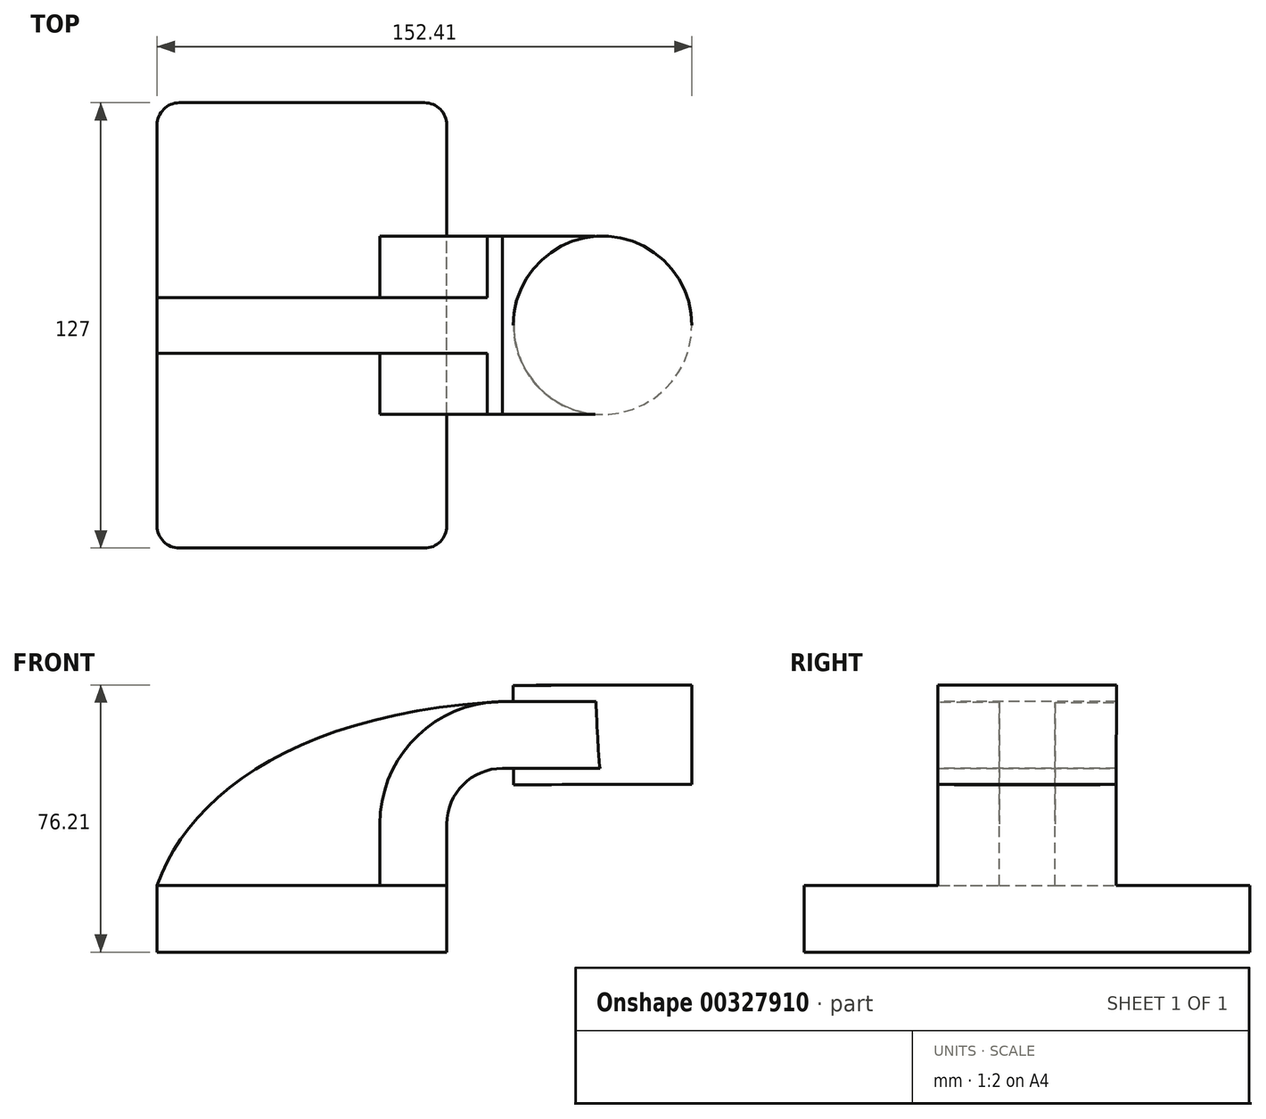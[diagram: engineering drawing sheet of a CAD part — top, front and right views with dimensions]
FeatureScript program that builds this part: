
annotation { "Feature Type Name" : "Feature", "Feature Type Description" : "" }
export const myFeature = defineFeature(function(context is Context, id is Id, definition is map)
    precondition{}
    {
        {
            var Q0;
            Q0=qCreatedBy(makeId("Front.planeOp"),FACE);
            var sketch = newSketch(context, id + "F0", { "sketchPlane" : qUnion([Q0])});
            skLineSegment(sketch, "E0.bottom", {"start": v(41.28, -9.52) * mm, "end": v(-41.28, -9.53) * mm});
            skLineSegment(sketch, "E0.top", {"start": v(41.28, 9.53) * mm, "end": v(-41.28, 9.53) * mm});
            skLineSegment(sketch, "E0.left", {"start": v(41.28, -9.52) * mm, "end": v(41.28, 9.53) * mm});
            skLineSegment(sketch, "E0.right", {"start": v(-41.28, -9.52) * mm, "end": v(-41.28, 9.53) * mm});
            skPoint(sketch, "E0.middle", {"position": v(0, 0) * mm});
            skLineSegment(sketch, "E1.bottom", {"start": v(111.12, 38.35) * mm, "end": v(60.32, 38.35) * mm});
            skLineSegment(sketch, "E1.top", {"start": v(111.12, 66.68) * mm, "end": v(60.33, 66.68) * mm});
            skLineSegment(sketch, "E1.left", {"start": v(111.12, 38.35) * mm, "end": v(111.12, 66.68) * mm});
            skLineSegment(sketch, "E1.right", {"start": v(60.33, 38.35) * mm, "end": v(60.33, 66.68) * mm});
            skPoint(sketch, "E1.middle", {"position": v(85.72, 52.51) * mm});
            skLineSegment(sketch, "E2", {"start": v(41.28, 9.53) * mm, "end": v(41.28, 27) * mm});
            skPoint(sketch, "E3.startSnap0", {"position": v(85.72, 38.35) * mm});
            skArc(sketch, "E4", {"start": v(57.15, 42.88) * mm, "mid": v(45.92, 38.23) * mm, "end": v(41.27, 27) * mm});
            skLineSegment(sketch, "E5", {"start": v(57.15, 42.88) * mm, "end": v(85.64, 42.88) * mm});
            skLineSegment(sketch, "E6.0", {"start": v(57.15, 61.93) * mm, "end": v(85.64, 61.93) * mm});
            skArc(sketch, "E6.1", {"start": v(57.15, 61.93) * mm, "mid": v(32.45, 51.7) * mm, "end": v(22.23, 27) * mm});
            skLineSegment(sketch, "E6.2", {"start": v(22.22, 9.53) * mm, "end": v(22.22, 27) * mm});
            skLineSegment(sketch, "E7", {"start": v(85.64, 66.68) * mm, "end": v(85.72, 38.35) * mm});
            skPoint(sketch, "E7.startSnap0", {"position": v(85.72, 66.68) * mm});
            skFitSpline(sketch, "E8", {"points": [v(-41.28, 9.53) * mm, v(57.15, 61.93) * mm], "startDerivative": vector(28, 79.75) * mm, "endDerivative": vector(171.45, 9.16) * mm});
            skLineSegment(sketch, "E9.bottom", {"start": v(85.64, 61.93) * mm, "end": v(57.15, 61.93) * mm});
            skLineSegment(sketch, "E9.top", {"start": v(85.64, 42.88) * mm, "end": v(57.15, 42.88) * mm});
            skLineSegment(sketch, "E9.left", {"start": v(85.64, 61.93) * mm, "end": v(85.64, 42.88) * mm});
            skLineSegment(sketch, "E9.right", {"start": v(57.15, 61.93) * mm, "end": v(57.15, 42.88) * mm});
            skSolve(sketch);
        }
        {
            var Q0;
            Q0=makeQuery(id+"F0.imprint","IMPRINT",FACE,{"disambiguationData":[TD([[makeQuery(id+"F0.imprint","IMPRINT",EDGE,{"derivedFrom":sQuery(id+"F0.wireOp",EDGE,"E0.bottom")}),-1.0]])]});
            extrude(context, id + "F1", {"entities" : qUnion([Q0]), "endBound" : BoundingType.SYMMETRIC, "depth" : 127 * mm});
        }
        {
            var Q0;
            {var subQ1=sQuery(id+"F0.wireOp",EDGE,"E2");Q0=makeQuery(id+"F0.imprint","IMPRINT",FACE,{"disambiguationData":[TD([[makeQuery(id+"F0.imprint","IMPRINT",EDGE,{"derivedFrom":subQ1}),1.0]])]});}
            extrude(context, id + "F2", {"entities" : qUnion([Q0]), "operationType" : NewBodyOperationType.ADD, "endBound" : BoundingType.SYMMETRIC, "depth" : 50.8 * mm});
        }
        {
            var Q0;
            {var subQ3=sQuery(id+"F0.wireOp",EDGE,"E6.2");Q0=makeQuery(id+"F0.imprint","IMPRINT",FACE,{"disambiguationData":[TD([[makeQuery(id+"F0.imprint","IMPRINT",EDGE,{"derivedFrom":subQ3}),1.0]])]});}
            extrude(context, id + "F3", {"entities" : qUnion([Q0]), "operationType" : NewBodyOperationType.ADD, "endBound" : BoundingType.SYMMETRIC, "depth" : 15.88 * mm});
        }
        {
            var Q0;
            {var subQ0=sQuery(id+"F0.wireOp",EDGE,"E1.left");Q0=makeQuery(id+"F0.imprint","IMPRINT",FACE,{"disambiguationData":[TD([[makeQuery(id+"F0.imprint","IMPRINT",EDGE,{"derivedFrom":subQ0}),1.0]])]});}
            var Q1;
            Q1=sQuery(id+"F0.wireOp",EDGE,"E7");
            revolve(context, id + "F4", {"operationType" : NewBodyOperationType.ADD, "entities" : qUnion([Q0]), "axis" : qUnion([Q1]), "revolveType" : RevolveType.FULL});
        }
        {
            var Q0;
            {var subQ5=sQuery(id+"F0.wireOp",EDGE,"E9.right");Q0=makeQuery(id+"F0.imprint","IMPRINT",FACE,{"disambiguationData":[TD([[makeQuery(id+"F0.imprint","IMPRINT",EDGE,{"derivedFrom":subQ5}),1.0]])]});}
            var Q1;
            {var subQ5=sQuery(id+"F0.wireOp",EDGE,"E9.left");Q1=makeQuery(id+"F0.imprint","IMPRINT",FACE,{"disambiguationData":[TD([[makeQuery(id+"F0.imprint","IMPRINT",EDGE,{"derivedFrom":subQ5}),-1.0]])]});}
            extrude(context, id + "F5", {"entities" : qUnion([Q0, Q1]), "operationType" : NewBodyOperationType.ADD, "endBound" : BoundingType.SYMMETRIC, "depth" : 50.8 * mm});
        }
        {
            var Q0;
            {var subQ0=sQuery(id+"F0.wireOp",EDGE,"E1.left");Q0=makeQuery(id+"F0.imprint","IMPRINT",FACE,{"disambiguationData":[TD([[makeQuery(id+"F0.imprint","IMPRINT",EDGE,{"derivedFrom":subQ0}),1.0]])]});}
            var Q1;
            Q1=sQuery(id+"F0.wireOp",EDGE,"E7");
            revolve(context, id + "F6", {"operationType" : NewBodyOperationType.ADD, "entities" : qUnion([Q0]), "axis" : qUnion([Q1]), "revolveType" : RevolveType.FULL});
        }
        {
            var Q0;
            Q0=makeQuery(id+"F1.opExtrude","CAP_EDGE",EDGE,{"disambiguationData":[OSD([sQuery(id+"F0.wireOp",EDGE,"E0.right")])],"isStart":false});
            var Q1;
            Q1=makeQuery(id+"F1.opExtrude","CAP_EDGE",EDGE,{"disambiguationData":[OSD([sQuery(id+"F0.wireOp",EDGE,"E0.left")])],"isStart":false});
            var Q2;
            Q2=makeQuery(id+"F1.opExtrude","CAP_EDGE",EDGE,{"disambiguationData":[OSD([sQuery(id+"F0.wireOp",EDGE,"E0.left")])],"isStart":true});
            var Q3;
            Q3=makeQuery(id+"F1.opExtrude","CAP_EDGE",EDGE,{"disambiguationData":[OSD([sQuery(id+"F0.wireOp",EDGE,"E0.right")])],"isStart":true});
            fillet(context, id + "F7", {"entities" : qUnion([Q0, Q1, Q2, Q3]), "radius" : 6.35 * mm, "tangentPropagation" : true, "allowEdgeOverflow" : false});
        }
    });
